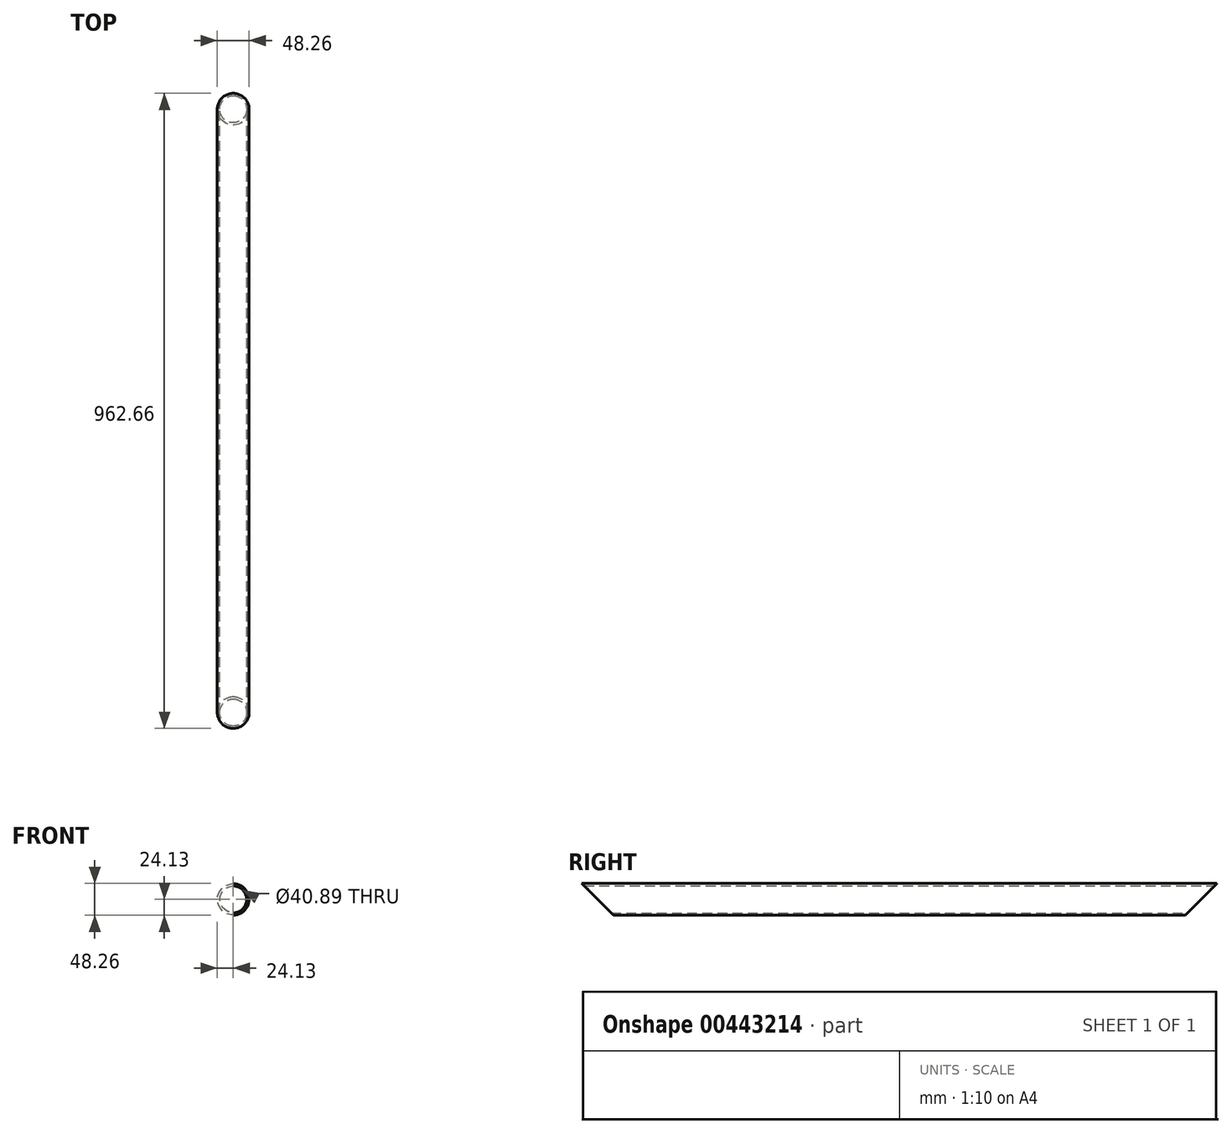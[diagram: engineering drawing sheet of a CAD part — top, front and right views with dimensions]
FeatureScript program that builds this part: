
annotation { "Feature Type Name" : "Feature", "Feature Type Description" : "" }
export const myFeature = defineFeature(function(context is Context, id is Id, definition is map)
    precondition{}
    {
        {
            var Q0;
            Q0=qCreatedBy(makeId("Front.planeOp"),FACE);
            var sketch = newSketch(context, id + "F0", { "sketchPlane" : qUnion([Q0])});
            skCircle(sketch, "E0", {"center": v(0, 0) * mm, "radius": 24.13 * mm});
            skCircle(sketch, "E1", {"center": v(0, 0) * mm, "radius": 20.45 * mm});
            skSolve(sketch);
        }
        {
            var Q0;
            Q0=makeQuery(id+"F0.imprint","IMPRINT",FACE,{"disambiguationData":[TD([[makeQuery(id+"F0.imprint","IMPRINT",EDGE,{"derivedFrom":sQuery(id+"F0.wireOp",EDGE,"E0")}),1.0]])]});
            extrude(context, id + "F1", {"entities" : qUnion([Q0]), "endBound" : BoundingType.SYMMETRIC, "depth" : 1016 * mm});
        }
        {
            var Q0;
            Q0=qCreatedBy(makeId("Right.planeOp"),FACE);
            var sketch = newSketch(context, id + "F2", { "sketchPlane" : qUnion([Q0])});
            skLineSegment(sketch, "E2", {"start": v(-457.2, 0) * mm, "end": v(-506.15, 48.95) * mm});
            skLineSegment(sketch, "E3", {"start": v(-506.15, 48.95) * mm, "end": v(-548.54, 25.52) * mm});
            skLineSegment(sketch, "E4", {"start": v(-548.54, 25.52) * mm, "end": v(-532.92, -70.43) * mm});
            skLineSegment(sketch, "E5", {"start": v(-532.92, -70.43) * mm, "end": v(-378.94, -78.26) * mm});
            skLineSegment(sketch, "E6", {"start": v(-457.2, 0) * mm, "end": v(-378.94, -78.26) * mm});
            skLineSegment(sketch, "E7.MirrorCS", {"start": v(548.54, 25.52) * mm, "end": v(532.92, -70.43) * mm});
            skLineSegment(sketch, "E8.MirrorCS", {"start": v(457.2, 0) * mm, "end": v(506.15, 48.95) * mm});
            skLineSegment(sketch, "E9.MirrorCS", {"start": v(532.92, -70.43) * mm, "end": v(378.94, -78.26) * mm});
            skLineSegment(sketch, "E10.MirrorCS", {"start": v(457.2, 0) * mm, "end": v(378.94, -78.26) * mm});
            skLineSegment(sketch, "E11.MirrorCS", {"start": v(506.15, 48.95) * mm, "end": v(548.54, 25.52) * mm});
            skSolve(sketch);
        }
        {
            var Q0;
            Q0 = qSketchRegion(id + "F2", true);
            extrude(context, id + "F3", {"entities" : qUnion([Q0]), "operationType" : NewBodyOperationType.REMOVE, "endBound" : BoundingType.SYMMETRIC, "oppositeDirection" : true, "depth" : 152.4 * mm});
        }
    });
